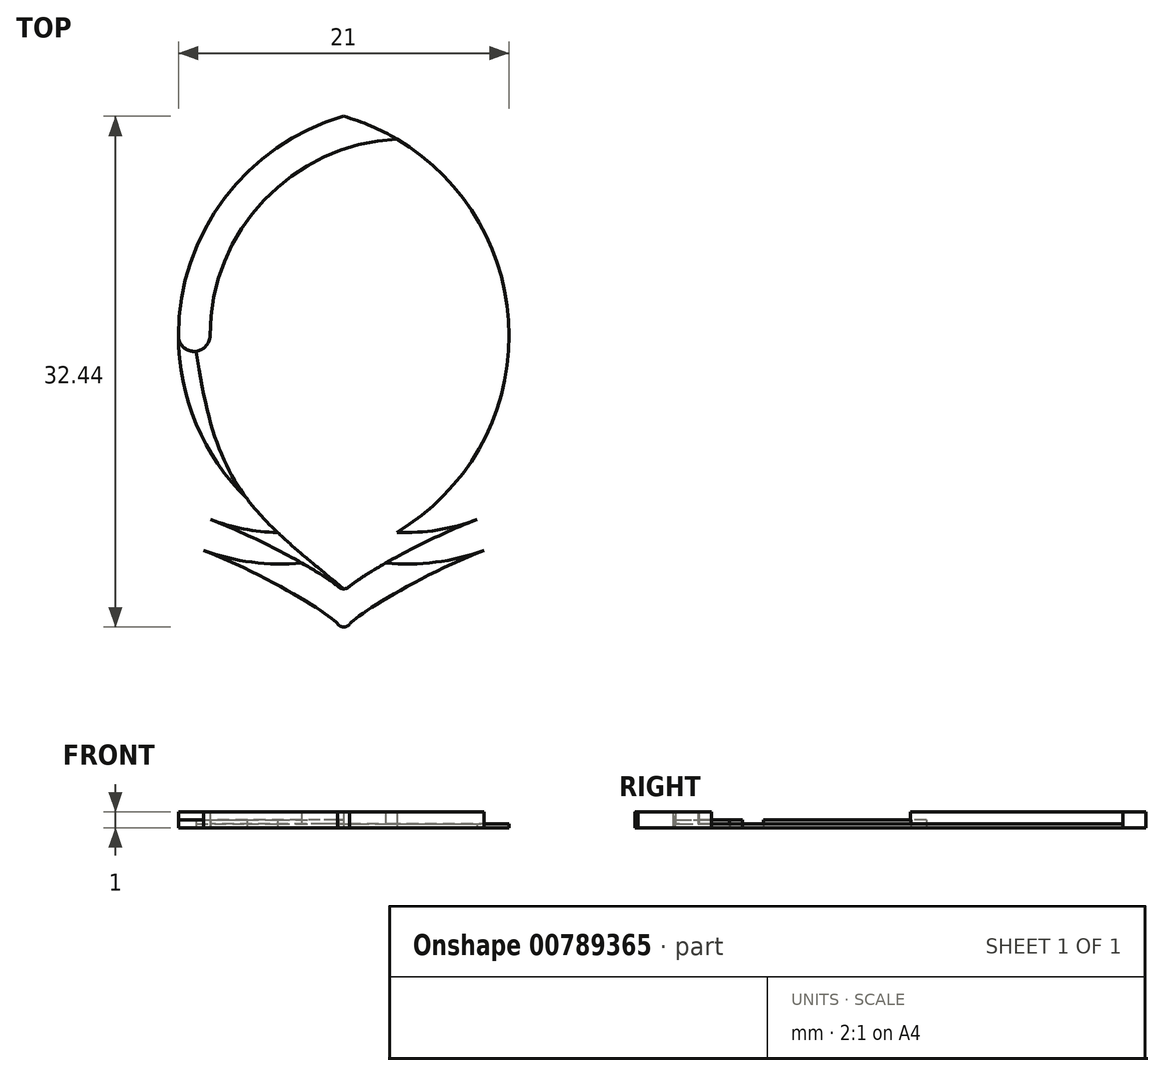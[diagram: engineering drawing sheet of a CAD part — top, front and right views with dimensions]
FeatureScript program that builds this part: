
annotation { "Feature Type Name" : "Feature", "Feature Type Description" : "" }
export const myFeature = defineFeature(function(context is Context, id is Id, definition is map)
    precondition{}
    {
        {
            var Q0;
            Q0=qCreatedBy(makeId("Top.planeOp"),FACE);
            var sketch = newSketch(context, id + "F0", { "sketchPlane" : qUnion([Q0])});
            skCircle(sketch, "E0", {"center": v(0, 0) * mm, "radius": 12.5 * mm});
            skLineSegment(sketch, "E1", {"start": v(0, 0) * mm, "end": v(-8, 0) * mm});
            skCircle(sketch, "E2", {"center": v(-8, 0) * mm, "radius": 12.5 * mm});
            skCircle(sketch, "E3.0", {"center": v(0, 0) * mm, "radius": 14.5 * mm});
            skCircle(sketch, "E4.0", {"center": v(-8, 0) * mm, "radius": 14.5 * mm});
            skLineSegment(sketch, "E5", {"start": v(-4, 0) * mm, "end": v(-4, -18) * mm});
            skCircle(sketch, "E6", {"center": v(-4, -18) * mm, "radius": 0.5 * mm});
            skFitSpline(sketch, "E7", {"points": [v(-4.38, -18.32) * mm, v(-12.9, -13.64) * mm], "startDerivative": vector(-1.16, 1.68) * mm, "endDerivative": vector(-11.98, 4.59) * mm});
            skFitSpline(sketch, "E8.MirrorCS", {"points": [v(-3.62, -18.32) * mm, v(4.9, -13.64) * mm], "startDerivative": vector(1.16, 1.68) * mm, "endDerivative": vector(11.98, 4.59) * mm});
            skLineSegment(sketch, "E9", {"start": v(-12.5, 0) * mm, "end": v(-14.5, 0) * mm});
            skCircle(sketch, "E10", {"center": v(-13.5, 0) * mm, "radius": 1 * mm});
            skFitSpline(sketch, "E11", {"points": [v(-4.02, -16.29) * mm, v(-12.5, -11.66) * mm], "startDerivative": vector(-0.88, 1.78) * mm, "endDerivative": vector(-11.98, 4.59) * mm});
            skFitSpline(sketch, "E12.MirrorCS", {"points": [v(-3.98, -16.29) * mm, v(4.5, -11.66) * mm], "startDerivative": vector(0.88, 1.78) * mm, "endDerivative": vector(11.98, 4.59) * mm});
            skLineSegment(sketch, "E13", {"start": v(-4, -15.57) * mm, "end": v(-3.16, -15.57) * mm});
            skCircle(sketch, "E14", {"center": v(-4, -15.57) * mm, "radius": 0.5 * mm});
            skFitSpline(sketch, "E15", {"points": [v(-13.5, 0) * mm, v(-4, -16.08) * mm], "startDerivative": vector(3.6, -28.74) * mm, "endDerivative": vector(18.2, -14.97) * mm});
            skSolve(sketch);
        }
        {
            var Q0;
            {var subQ6=sQuery(id+"F0.wireOp",EDGE,"E0");var subQ7=makeQuery(id+"F0.imprint","IMPRINT",VERTEX,{"derivedFrom":subQ6});Q0=makeQuery(id+"F0.imprint","IMPRINT",FACE,{"disambiguationData":[TD([[makeQuery(id+"F0.imprint","IMPRINT",EDGE,{"disambiguationData":[TD([[subQ7,1.0]])],"derivedFrom":subQ6}),-1.0]])]});}
            var Q1;
            {var subQ0=sQuery(id+"F0.wireOp",EDGE,"E8.MirrorCS");var subQ1=sQuery(id+"F0.wireOp",EDGE,"E3.0");var subQ2=makeQuery(id+"F0.imprint","INTERSECT",VERTEX,{"derivedFrom":[subQ1,subQ0]});Q1=makeQuery(id+"F0.imprint","IMPRINT",FACE,{"disambiguationData":[TD([[makeQuery(id+"F0.imprint","IMPRINT",EDGE,{"disambiguationData":[TD([[subQ2,1.0]])],"derivedFrom":subQ1}),-1.0]])]});}
            var Q2;
            {var subQ3=sQuery(id+"F0.wireOp",EDGE,"E7");var subQ7=sQuery(id+"F0.wireOp",EDGE,"E4.0");var subQ8=makeQuery(id+"F0.imprint","INTERSECT",VERTEX,{"derivedFrom":[subQ7,subQ3]});Q2=makeQuery(id+"F0.imprint","IMPRINT",FACE,{"disambiguationData":[TD([[makeQuery(id+"F0.imprint","IMPRINT",EDGE,{"disambiguationData":[TD([[subQ8,-1.0]])],"derivedFrom":subQ7}),-1.0]])]});}
            var Q3;
            {var subQ0=sQuery(id+"F0.wireOp",EDGE,"E6");var subQ1=makeQuery(id+"F0.imprint","INTERSECT",VERTEX,{"derivedFrom":[sQuery(id+"F0.wireOp",EDGE,"E5"),subQ0]});Q3=makeQuery(id+"F0.imprint","IMPRINT",FACE,{"disambiguationData":[TD([[makeQuery(id+"F0.imprint","IMPRINT",EDGE,{"disambiguationData":[TD([[subQ1,-1.0]])],"derivedFrom":subQ0}),1.0]])]});}
            var Q4;
            {var subQ2=sQuery(id+"F0.wireOp",EDGE,"E0");var subQ4=sQuery(id+"F0.wireOp",EDGE,"E2");var subQ5=makeQuery(id+"F0.imprint","INTERSECT",VERTEX,{"derivedFrom":[subQ2,subQ4]});Q4=makeQuery(id+"F0.imprint","IMPRINT",FACE,{"disambiguationData":[TD([[makeQuery(id+"F0.imprint","IMPRINT",EDGE,{"disambiguationData":[TD([[subQ5,-1.0]])],"derivedFrom":subQ4}),1.0]])]});}
            var Q5;
            {var subQ0=sQuery(id+"F0.wireOp",EDGE,"E2");var subQ1=sQuery(id+"F0.wireOp",EDGE,"E0");var subQ2=makeQuery(id+"F0.imprint","INTERSECT",VERTEX,{"derivedFrom":[subQ1,subQ0]});Q5=makeQuery(id+"F0.imprint","IMPRINT",FACE,{"disambiguationData":[TD([[makeQuery(id+"F0.imprint","IMPRINT",EDGE,{"disambiguationData":[TD([[subQ2,1.0]])],"derivedFrom":subQ1}),-1.0]])]});}
            var Q6;
            {var subQ5=sQuery(id+"F0.wireOp",EDGE,"E2");var subQ7=makeQuery(id+"F0.imprint","IMPRINT",VERTEX,{"derivedFrom":subQ5});Q6=makeQuery(id+"F0.imprint","IMPRINT",FACE,{"disambiguationData":[TD([[makeQuery(id+"F0.imprint","IMPRINT",EDGE,{"disambiguationData":[TD([[subQ7,1.0]])],"derivedFrom":subQ5}),-1.0]])]});}
            var Q7;
            {var subQ0=sQuery(id+"F0.wireOp",EDGE,"E9");Q7=makeQuery(id+"F0.imprint","IMPRINT",FACE,{"disambiguationData":[TD([[makeQuery(id+"F0.imprint","IMPRINT",EDGE,{"derivedFrom":subQ0}),1.0]])]});}
            var Q8;
            {var subQ0=sQuery(id+"F0.wireOp",EDGE,"E9");Q8=makeQuery(id+"F0.imprint","IMPRINT",FACE,{"disambiguationData":[TD([[makeQuery(id+"F0.imprint","IMPRINT",EDGE,{"derivedFrom":subQ0}),-1.0]])]});}
            extrude(context, id + "F1", {"entities" : qUnion([Q0, Q1, Q2, Q3, Q4, Q5, Q6, Q7, Q8]), "depth" : 1 * mm, "offsetDistance" : 25 * mm});
        }
        {
            var Q0;
            {var subQ2=sQuery(id+"F0.wireOp",EDGE,"E2");var subQ7=makeQuery(id+"F0.imprint","IMPRINT",VERTEX,{"derivedFrom":subQ2});Q0=makeQuery(id+"F0.imprint","IMPRINT",FACE,{"disambiguationData":[TD([[makeQuery(id+"F0.imprint","IMPRINT",EDGE,{"disambiguationData":[TD([[subQ7,1.0]])],"derivedFrom":subQ2}),1.0]])]});}
            var Q1;
            {var subQ1=sQuery(id+"F0.wireOp",EDGE,"E3.0");var subQ3=sQuery(id+"F0.wireOp",EDGE,"E15");var subQ4=makeQuery(id+"F0.imprint","INTERSECT",VERTEX,{"derivedFrom":[subQ1,subQ3]});Q1=makeQuery(id+"F0.imprint","IMPRINT",FACE,{"disambiguationData":[TD([[makeQuery(id+"F0.imprint","IMPRINT",EDGE,{"disambiguationData":[TD([[subQ4,1.0]])],"derivedFrom":subQ3}),-1.0]])]});}
            var Q2;
            {var subQ0=sQuery(id+"F0.wireOp",EDGE,"E11");var subQ1=sQuery(id+"F0.wireOp",EDGE,"E2");var subQ2=makeQuery(id+"F0.imprint","INTERSECT",VERTEX,{"derivedFrom":[subQ1,subQ0]});Q2=makeQuery(id+"F0.imprint","IMPRINT",FACE,{"disambiguationData":[TD([[makeQuery(id+"F0.imprint","IMPRINT",EDGE,{"disambiguationData":[TD([[subQ2,-1.0]])],"derivedFrom":subQ1}),-1.0]])]});}
            var Q3;
            {var subQ0=sQuery(id+"F0.wireOp",EDGE,"E11");var subQ1=sQuery(id+"F0.wireOp",EDGE,"E4.0");var subQ2=makeQuery(id+"F0.imprint","INTERSECT",VERTEX,{"derivedFrom":[subQ1,subQ0]});Q3=makeQuery(id+"F0.imprint","IMPRINT",FACE,{"disambiguationData":[TD([[makeQuery(id+"F0.imprint","IMPRINT",EDGE,{"disambiguationData":[TD([[subQ2,-1.0]])],"derivedFrom":subQ1}),-1.0]])]});}
            var Q4;
            {var subQ0=sQuery(id+"F0.wireOp",EDGE,"E14");var subQ1=sQuery(id+"F0.wireOp",EDGE,"E11");var subQ2=makeQuery(id+"F0.imprint","INTERSECT",VERTEX,{"disambiguationData":[OD(0.0)],"derivedFrom":[subQ1,subQ0]});Q4=makeQuery(id+"F0.imprint","IMPRINT",FACE,{"disambiguationData":[TD([[makeQuery(id+"F0.imprint","IMPRINT",EDGE,{"disambiguationData":[TD([[subQ2,-1.0]])],"derivedFrom":subQ1}),-1.0]])]});}
            extrude(context, id + "F2", {"entities" : qUnion([Q0, Q1, Q2, Q3, Q4]), "depth" : .5 * mm, "offsetDistance" : 25 * mm});
        }
        {
            var Q0;
            {var subQ0=sQuery(id+"F0.wireOp",EDGE,"E0");var subQ2=sQuery(id+"F0.wireOp",EDGE,"E2");var subQ3=makeQuery(id+"F0.imprint","INTERSECT",VERTEX,{"derivedFrom":[subQ0,subQ2]});Q0=makeQuery(id+"F0.imprint","IMPRINT",FACE,{"disambiguationData":[TD([[makeQuery(id+"F0.imprint","IMPRINT",EDGE,{"disambiguationData":[TD([[subQ3,-1.0]])],"derivedFrom":subQ0}),1.0]])]});}
            var Q1;
            {var subQ5=sQuery(id+"F0.wireOp",EDGE,"E3.0");var subQ6=sQuery(id+"F0.wireOp",EDGE,"E2");var subQ7=makeQuery(id+"F0.imprint","INTERSECT",VERTEX,{"disambiguationData":[OD(1.0)],"derivedFrom":[subQ6,subQ5]});Q1=makeQuery(id+"F0.imprint","IMPRINT",FACE,{"disambiguationData":[TD([[makeQuery(id+"F0.imprint","IMPRINT",EDGE,{"disambiguationData":[TD([[subQ7,1.0]])],"derivedFrom":subQ5}),1.0]])]});}
            var Q2;
            {var subQ0=sQuery(id+"F0.wireOp",EDGE,"E2");var subQ1=sQuery(id+"F0.wireOp",EDGE,"E0");var subQ2=makeQuery(id+"F0.imprint","INTERSECT",VERTEX,{"derivedFrom":[subQ1,subQ0]});Q2=makeQuery(id+"F0.imprint","IMPRINT",FACE,{"disambiguationData":[TD([[makeQuery(id+"F0.imprint","IMPRINT",EDGE,{"disambiguationData":[TD([[subQ2,1.0]])],"derivedFrom":subQ1}),1.0]])]});}
            var Q3;
            {var subQ0=sQuery(id+"F0.wireOp",EDGE,"E0");var subQ4=makeQuery(id+"F0.imprint","IMPRINT",VERTEX,{"derivedFrom":subQ0});Q3=makeQuery(id+"F0.imprint","IMPRINT",FACE,{"disambiguationData":[TD([[makeQuery(id+"F0.imprint","IMPRINT",EDGE,{"disambiguationData":[TD([[subQ4,1.0]])],"derivedFrom":subQ0}),1.0]])]});}
            var Q4;
            {var subQ0=sQuery(id+"F0.wireOp",EDGE,"E4.0");var subQ1=sQuery(id+"F0.wireOp",EDGE,"E0");var subQ2=makeQuery(id+"F0.imprint","INTERSECT",VERTEX,{"disambiguationData":[OD(1.0)],"derivedFrom":[subQ1,subQ0]});Q4=makeQuery(id+"F0.imprint","IMPRINT",FACE,{"disambiguationData":[TD([[makeQuery(id+"F0.imprint","IMPRINT",EDGE,{"disambiguationData":[TD([[subQ2,1.0]])],"derivedFrom":subQ1}),-1.0]])]});}
            var Q5;
            {var subQ0=sQuery(id+"F0.wireOp",EDGE,"E3.0");var subQ1=sQuery(id+"F0.wireOp",EDGE,"E2");var subQ2=makeQuery(id+"F0.imprint","INTERSECT",VERTEX,{"disambiguationData":[OD(1.0)],"derivedFrom":[subQ1,subQ0]});Q5=makeQuery(id+"F0.imprint","IMPRINT",FACE,{"disambiguationData":[TD([[makeQuery(id+"F0.imprint","IMPRINT",EDGE,{"disambiguationData":[TD([[subQ2,-1.0]])],"derivedFrom":subQ1}),-1.0]])]});}
            var Q6;
            {var subQ0=sQuery(id+"F0.wireOp",EDGE,"E15");var subQ1=sQuery(id+"F0.wireOp",EDGE,"E2");var subQ2=makeQuery(id+"F0.imprint","INTERSECT",VERTEX,{"derivedFrom":[subQ1,subQ0]});Q6=makeQuery(id+"F0.imprint","IMPRINT",FACE,{"disambiguationData":[TD([[makeQuery(id+"F0.imprint","IMPRINT",EDGE,{"disambiguationData":[TD([[subQ2,-1.0]])],"derivedFrom":subQ1}),-1.0]])]});}
            var Q7;
            {var subQ3=sQuery(id+"F0.wireOp",EDGE,"E5");var subQ5=sQuery(id+"F0.wireOp",EDGE,"E14");var subQ6=makeQuery(id+"F0.imprint","INTERSECT",VERTEX,{"derivedFrom":[subQ3,subQ5]});Q7=makeQuery(id+"F0.imprint","IMPRINT",FACE,{"disambiguationData":[TD([[makeQuery(id+"F0.imprint","IMPRINT",EDGE,{"disambiguationData":[TD([[subQ6,-1.0]])],"derivedFrom":subQ5}),-1.0]])]});}
            var Q8;
            {var subQ0=sQuery(id+"F0.wireOp",EDGE,"E12.MirrorCS");var subQ1=sQuery(id+"F0.wireOp",EDGE,"E0");var subQ2=makeQuery(id+"F0.imprint","INTERSECT",VERTEX,{"derivedFrom":[subQ1,subQ0]});Q8=makeQuery(id+"F0.imprint","IMPRINT",FACE,{"disambiguationData":[TD([[makeQuery(id+"F0.imprint","IMPRINT",EDGE,{"disambiguationData":[TD([[subQ2,1.0]])],"derivedFrom":subQ1}),-1.0]])]});}
            var Q9;
            {var subQ0=sQuery(id+"F0.wireOp",EDGE,"E15");var subQ1=sQuery(id+"F0.wireOp",EDGE,"E2");var subQ2=makeQuery(id+"F0.imprint","INTERSECT",VERTEX,{"derivedFrom":[subQ1,subQ0]});Q9=makeQuery(id+"F0.imprint","IMPRINT",FACE,{"disambiguationData":[TD([[makeQuery(id+"F0.imprint","IMPRINT",EDGE,{"disambiguationData":[TD([[subQ2,-1.0]])],"derivedFrom":subQ1}),1.0]])]});}
            var Q10;
            {var subQ0=sQuery(id+"F0.wireOp",EDGE,"E5");var subQ1=makeQuery(id+"F0.imprint","INTERSECT",VERTEX,{"derivedFrom":[subQ0,sQuery(id+"F0.wireOp",EDGE,"E13")]});Q10=makeQuery(id+"F0.imprint","IMPRINT",FACE,{"disambiguationData":[TD([[makeQuery(id+"F0.imprint","IMPRINT",EDGE,{"disambiguationData":[TD([[subQ1,1.0]])],"derivedFrom":subQ0}),-1.0]])]});}
            var Q11;
            {var subQ0=sQuery(id+"F0.wireOp",EDGE,"E13");var subQ1=sQuery(id+"F0.wireOp",EDGE,"E5");var subQ2=makeQuery(id+"F0.imprint","INTERSECT",VERTEX,{"derivedFrom":[subQ1,subQ0]});Q11=makeQuery(id+"F0.imprint","IMPRINT",FACE,{"disambiguationData":[TD([[makeQuery(id+"F0.imprint","IMPRINT",EDGE,{"disambiguationData":[TD([[subQ2,1.0]])],"derivedFrom":subQ1}),1.0]])]});}
            var Q12;
            {var subQ0=sQuery(id+"F0.wireOp",EDGE,"E13");var subQ1=sQuery(id+"F0.wireOp",EDGE,"E12.MirrorCS");var subQ2=makeQuery(id+"F0.imprint","INTERSECT",VERTEX,{"derivedFrom":[subQ1,subQ0]});Q12=makeQuery(id+"F0.imprint","IMPRINT",FACE,{"disambiguationData":[TD([[makeQuery(id+"F0.imprint","IMPRINT",EDGE,{"disambiguationData":[TD([[subQ2,-1.0]])],"derivedFrom":subQ1}),1.0]])]});}
            var Q13;
            {var subQ3=sQuery(id+"F0.wireOp",EDGE,"E14");var subQ5=sQuery(id+"F0.wireOp",EDGE,"E12.MirrorCS");var subQ6=makeQuery(id+"F0.imprint","INTERSECT",VERTEX,{"disambiguationData":[OD(0.0)],"derivedFrom":[subQ5,subQ3]});Q13=makeQuery(id+"F0.imprint","IMPRINT",FACE,{"disambiguationData":[TD([[makeQuery(id+"F0.imprint","IMPRINT",EDGE,{"disambiguationData":[TD([[subQ6,-1.0]])],"derivedFrom":subQ5}),1.0]])]});}
            var Q14;
            {var subQ0=sQuery(id+"F0.wireOp",EDGE,"E13");var subQ1=sQuery(id+"F0.wireOp",EDGE,"E12.MirrorCS");var subQ2=makeQuery(id+"F0.imprint","INTERSECT",VERTEX,{"derivedFrom":[subQ1,subQ0]});Q14=makeQuery(id+"F0.imprint","IMPRINT",FACE,{"disambiguationData":[TD([[makeQuery(id+"F0.imprint","IMPRINT",EDGE,{"disambiguationData":[TD([[subQ2,1.0]])],"derivedFrom":subQ1}),1.0]])]});}
            extrude(context, id + "F3", {"entities" : qUnion([Q0, Q1, Q2, Q3, Q4, Q5, Q6, Q7, Q8, Q9, Q10, Q11, Q12, Q13, Q14]), "depth" : .25 * mm, "offsetDistance" : 25 * mm});
        }
    });
